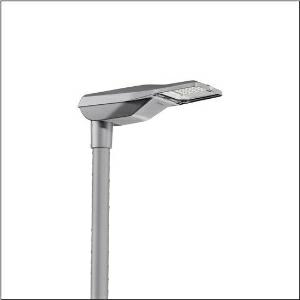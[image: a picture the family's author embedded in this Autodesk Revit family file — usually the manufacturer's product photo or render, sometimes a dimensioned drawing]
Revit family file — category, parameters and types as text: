
# Revit family: streetlight_sl_21_iq_micro___st1_0ab_5xe1m31g08cb_01f6
name_source: partatom
category: Lighting Fixtures
units: mm (PartAtom-declared; Revit-internal decimal feet)

## family parameters
Cut with Voids When Loaded = No
Host = Face
Light Source = No
Part Type = Normal
Room Calculation Point = No
Round Connector Dimension = Use Diameter
Shared = No

## types (1)
- --- (1 x LED, 2520 lm, 19.4 W, 3000K)
    Apparent Load = 19 VA
    CIE Flux Codes = 38 73 97 100 100
    Color Rendering = 70
    Color Temperature = 3000K
    Default Elevation = 1800 mm
    Description = Streetlight SL 21 iQ micro, mast luminaire, primary light control with lens, of PMMA, primary optical cover: cover, of toughened safety glass, transparent, light distribution: ST1.0aB, light emission: direct distribution, primary light characteristic: asymmetric, installation type: post-top, side-entry, LED, High Power LED, rated luminous flux: 2.520lm, luminous efficacy: 130lm/W, light colour: 730, colour temperature: 3000K, control gear: iQ Street-Remote, control: Street-Remote, Auto-Match, Temp-Guard, Lumen-Switch, Night-Set, Smart-Wire, Light-Fading, Desk-Remote (wireless, voltage-free reading and setting of iQ features in the workshop via application-optimized NFC function/RFID function), optimised constant luminous flux control (CLO 2.0), pre-setting: linear dimming characteristic, mains connection: 220..240V, AC, 50/60Hz, start of lifetime: 19W, end of service life: 20W, reduction: 10W, luminaire housing, of diecast aluminium, powder-coated, Siteco® metallic grey (DB 702S), corrosivity category C5 mid according to DIN EN ISO 12944, please order mast flange separately, inclination adjustable: 0°, 5°, 10°, 15°, sealing non-destructively replaceable, multi-level sealing system, length: 528mm, width: 235mm, height: 110mm, mast flange for spigot size: 42mm (side-entry): 5XC10008XM4, 60/48mm (side-entry/post-top): 5XC10108XM2, 76/60mm (side-entry/post-top): 5XC10108XM1, protection rating (complete): IP66, insulation class (complete): insulation class II (safety insulation), certification: CE, ENEC, ENEC+, VDE, impact resistance: IK10, permissible operating ambient temperature for outdoor applications: -40..+50°C, standard-compliant lighting for roads and squares, packaging unit: 1 piece

Light Distribution: ST1.0aB
    Height = 110 mm
    Lamp = 1 x LED
    Lamp Light Flux = 2520 lm
    Lamp Power = 19.4 W
    Lamp count = 1
    Length = 528 mm
    Luminous efficacy = 130 lm/W
    Manufacturer = Siteco
    ModVariant = No
    Model = 5XE1M31G08CB
    Number of Poles = 1
    OnlyDefault = Yes
    Power Factor = 1
    Product Name = Streetlight SL 21 iQ micro | ST1.0aB
    Product group = mast luminaire | pylon top
    ProductGroupID = 6100
    Protection Class = Protection class II
    Protection Degree = IP 66
    RLX_Detail_Level = 1
    RLX_Emergency_Light_Flux = 0 lm
    RLX_Emergency_Type = 0
    RLX_Emergency_Type_DB = No
    RlxData = <blob elided: 98469 chars, md5=a18eb81f>
    Socket = socket
    Standby Power = 0 W
    System Light Flux = 2520 lm
    System Power = 19 W
    Type Comments = factory setting: luminous flux: 100 % | dim-lin: 254 | 387 mA
    Type Image = l_1006881.jpg
    URL = http://relux.com
    VarID = @adj_159623
    Voltage = 0 V
    Weight = 0.00 kg
    Width = 235 mm

## geometry (parser evidence)
native form markers: Blend x4, Sweep x10
no freeform markers — native parametric forms only
